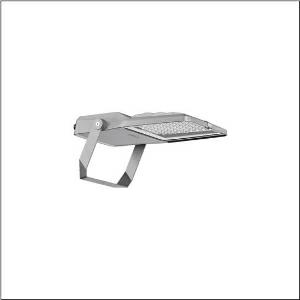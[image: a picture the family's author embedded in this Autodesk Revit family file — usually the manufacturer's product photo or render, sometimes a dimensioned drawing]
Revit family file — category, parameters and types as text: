
# Revit family: floodlight_fl_21_iq_mini___pl64_5xa7772c4e1a_6403
name_source: partatom
category: Lighting Fixtures
units: mm (PartAtom-declared; Revit-internal decimal feet)

## family parameters
Cut with Voids When Loaded = No
Host = Face
Light Source = No
Part Type = Normal
Room Calculation Point = No
Round Connector Dimension = Use Diameter
Shared = No

## types (1)
- --- (1 x LED, 12280 lm, 87.2 W, 4000K)
    Apparent Load = 87 VA
    CIE Flux Codes = 28 80 98 100 100
    Color Rendering = 70
    Color Temperature = 4000K
    Default Elevation = 1800 mm
    Description = Floodlight FL 21 iQ mini, floodlight, primary light control with lens, of PMMA, primary optical cover: protective disc, of toughened safety glass, transparent, light distribution: PL64, light emission: direct distribution, installation type: surface-mounted, LED, High Power LED, rated luminous flux: 12.280lm, luminous efficacy: 141lm/W, light colour: 740, colour temperature: 4000K, control gear: iQ Street-Remote/DALI, control: Street-Remote, Auto-Match, Temp-Guard, Night-Set, Smart-Wire, Desk-Remote (wireless, voltage-free reading and setting of iQ features in the workshop via application-optimized NFC function/RFID function), optimised constant luminous flux control (CLO 2.0), with terminal, 6-pole, mains connection: 220..240V, AC, 50/60Hz, start of lifetime: 87W, end of service life: 92W, reduction: 40W, luminaire housing, of diecast aluminium, powder-coated, Siteco® metallic grey (DB 702S), corrosivity category C5 mid according to DIN EN ISO 12944, suitable for swimming pools, chlorine-resistant, sealing non-destructively replaceable, mounting bracket, of steel, galvanised, powder-coated, Siteco® metallic grey (DB 702S), protection rating (complete): IP66, insulation class (complete): insulation class II (safety insulation), certification: CE, ENEC, VDE, protection symbol: D, impact resistance: IK08, permissible operating ambient temperature: -40..+40°C, permissible operating ambient temperature for outdoor applications: -40..+50°C, standard: DIN EN 12944, LABS conformity tested according to VDMA 24364:2018-05, packaging unit: 1 piece

Light Distribution: PL64
    Height = 70 mm
    Lamp = 1 x LED
    Lamp Light Flux = 12280 lm
    Lamp Power = 87.2 W
    Lamp count = 1
    Length = 485 mm
    Luminous efficacy = 141 lm/W
    Manufacturer = Siteco
    ModVariant = No
    Model = 5XA7772C4E1A
    Number of Poles = 1
    OnlyDefault = Yes
    Power Factor = 1
    Product Name = Floodlight FL 21 iQ mini | PL64
    Product group = floodlight | pylon annexe
    ProductGroupID = 6200
    Protection Class = Protection class II
    Protection Degree = IP 66
    RLX_Detail_Level = 1
    RLX_Emergency_Light_Flux = 0 lm
    RLX_Emergency_Type = 0
    RLX_Emergency_Type_DB = No
    RlxData = <blob elided: 96221 chars, md5=d2dd374f>
    Socket = socket
    Standby Power = 0 W
    System Light Flux = 12280 lm
    System Power = 87 W
    Type Comments = factory setting: luminous flux: 100 % | dim-lin: 254 | 456 mA
    Type Image = l_1006845.jpg
    URL = http://relux.com
    VarID = @adj_166290
    Voltage = 0 V
    Weight = 0.00 kg
    Width = 337 mm

## geometry (parser evidence)
native form markers: Blend x4, Sweep x12
no freeform markers — native parametric forms only
